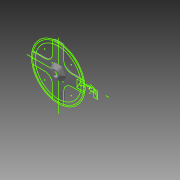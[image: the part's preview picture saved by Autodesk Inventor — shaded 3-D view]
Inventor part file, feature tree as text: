
AUTODESK INVENTOR PART (.ipt)
format: ipt  version: 2014 SP2 (Build 180246200, 246)  size: 241,664 bytes
history: native  units: mm
features: extrude x2, fillet x2, sketch x1, chamfer x1
ambient origin geometry x8: Origin, YZ Plane, XZ Plane, XY Plane, X Axis, Y Axis, Z Axis, Center Point
bodies: Solid1 (feature_tree)
feature tree (6):
  sketch  "Sketch1"  dims[d0=19.0mm d1=52.5mm d2=0.5mm d3=0.5mm d4=0.5mm d5=9.0mm d6=9.65mm d7=9.65mm d8=9.35mm d9=100.0mm d10=135.0mm d11=3.0mm d12=0.0mm d13=14.0mm d14=14.0mm d15=10.5mm d16=17.0mm d17=19.7mm d18=18.0mm d19=21.4mm d20=24.55mm d21=27.95mm d22=34.5mm d23=35.5mm d24=42.0mm d25=28.0mm d26=28.0mm d27=20.0mm d28=20.0mm d29=20.0mm d30=20.0mm d31=13.8mm d32=3.0mm d33=8.0mm d34=0.0mm d35=8.0mm d36=2.0mm d37=45.0deg d38=10.0mm d39=2.5mm d40=2.5mm d41=2.5mm d42=2.5mm d43=2.5mm d44=2.5mm d45=2.5mm d46=5.0mm]
  extrude  "Extrusion1"  Depth=5.0mm
  extrude  "Extrusion2"  Depth=5.0mm
  chamfer  "Chamfer1"  Distance=0.5mm
  fillet  "Fillet1"  Radius=9.0mm
  fillet  "Fillet2"  Radius=9.65mm
